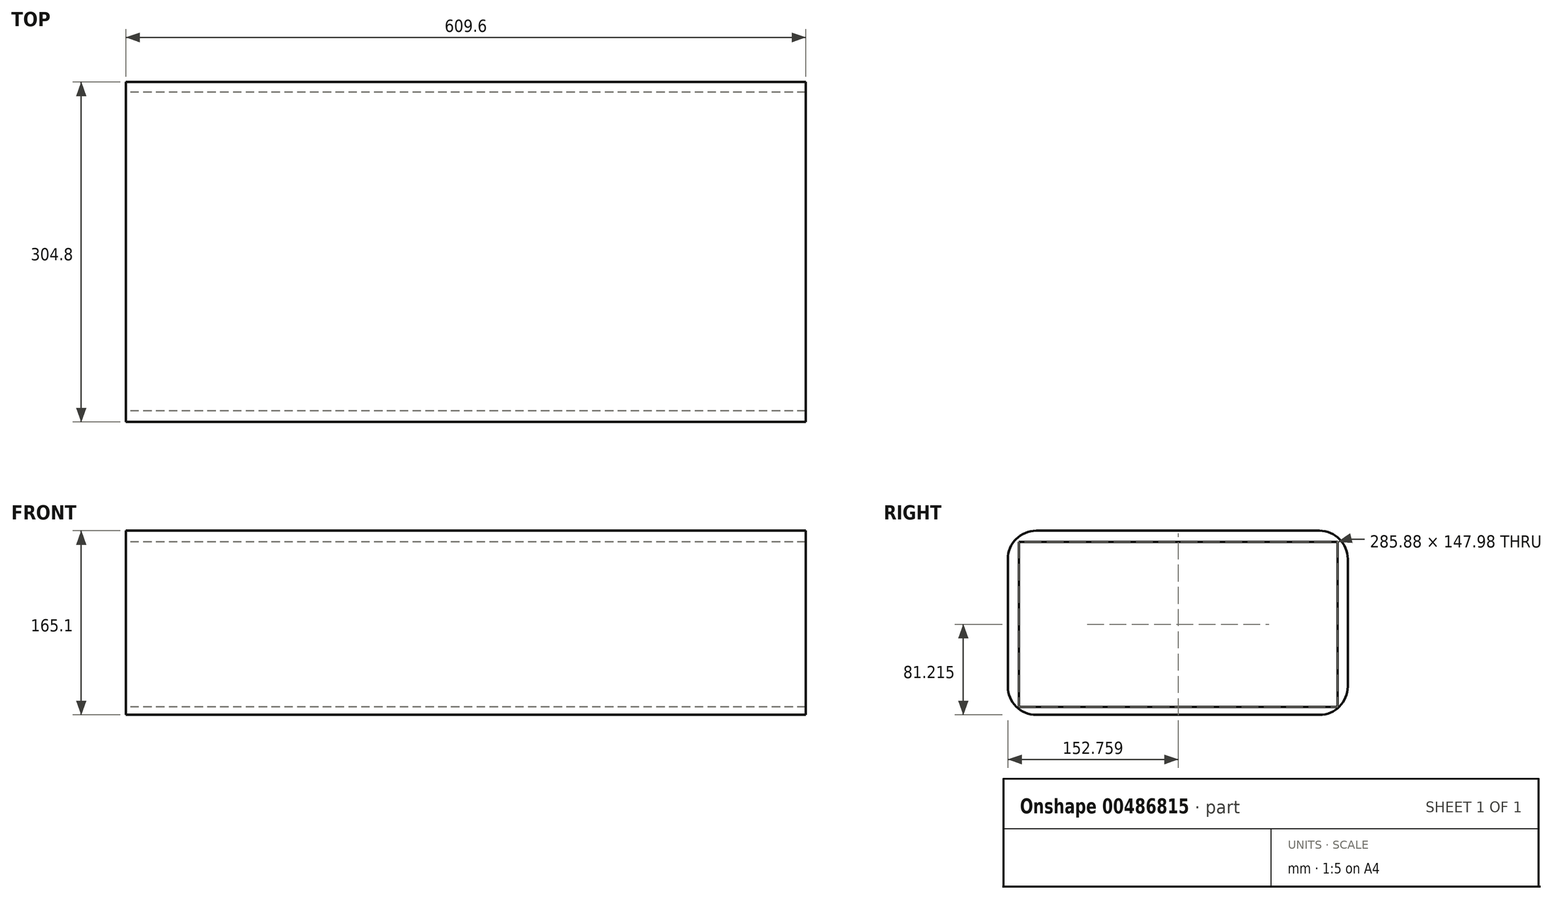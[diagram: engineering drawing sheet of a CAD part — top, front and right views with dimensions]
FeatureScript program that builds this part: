
annotation { "Feature Type Name" : "Feature", "Feature Type Description" : "" }
export const myFeature = defineFeature(function(context is Context, id is Id, definition is map)
    precondition{}
    {
        {
            var Q0;
            Q0=qCreatedBy(makeId("Right.planeOp"),FACE);
            var sketch = newSketch(context, id + "F0", { "sketchPlane" : qUnion([Q0])});
            skLineSegment(sketch, "E0.bottom", {"start": v(-140.28, 53.64) * mm, "end": v(164.52, 53.64) * mm});
            skLineSegment(sketch, "E0.top", {"start": v(-140.28, -111.46) * mm, "end": v(164.52, -111.46) * mm});
            skLineSegment(sketch, "E0.left", {"start": v(-140.28, 53.64) * mm, "end": v(-140.28, -111.46) * mm});
            skLineSegment(sketch, "E0.right", {"start": v(164.52, 53.64) * mm, "end": v(164.52, -111.46) * mm});
            skLineSegment(sketch, "E1.bottom", {"start": v(-130.46, 43.74) * mm, "end": v(155.42, 43.74) * mm});
            skLineSegment(sketch, "E1.top", {"start": v(-130.46, -104.24) * mm, "end": v(155.42, -104.24) * mm});
            skLineSegment(sketch, "E1.left", {"start": v(-130.46, 43.74) * mm, "end": v(-130.46, -104.24) * mm});
            skLineSegment(sketch, "E1.right", {"start": v(155.42, 43.74) * mm, "end": v(155.42, -104.24) * mm});
            skSolve(sketch);
        }
        {
            var Q0;
            Q0=makeQuery(id+"F0.imprint","IMPRINT",FACE,{"disambiguationData":[TD([[makeQuery(id+"F0.imprint","IMPRINT",EDGE,{"derivedFrom":sQuery(id+"F0.wireOp",EDGE,"E0.bottom")}),-1.0]])]});
            extrude(context, id + "F1", {"entities" : qUnion([Q0]), "depth" : 609.6 * mm, "offsetDistance" : 25.4 * mm});
        }
        {
            var Q0;
            Q0=makeQuery(id+"F1.opExtrude","SWEPT_EDGE",EDGE,{"disambiguationData":[OSD([sQuery(id+"F0.wireOp",EDGE,"E0.bottom"),sQuery(id+"F0.wireOp",EDGE,"E0.left")])]});
            var Q1;
            Q1=makeQuery(id+"F1.opExtrude","SWEPT_EDGE",EDGE,{"disambiguationData":[OSD([sQuery(id+"F0.wireOp",EDGE,"E0.bottom"),sQuery(id+"F0.wireOp",EDGE,"E0.right")])]});
            var Q2;
            Q2=makeQuery(id+"F1.opExtrude","SWEPT_EDGE",EDGE,{"disambiguationData":[OSD([sQuery(id+"F0.wireOp",EDGE,"E0.top"),sQuery(id+"F0.wireOp",EDGE,"E0.left")])]});
            var Q3;
            Q3=makeQuery(id+"F1.opExtrude","SWEPT_EDGE",EDGE,{"disambiguationData":[OSD([sQuery(id+"F0.wireOp",EDGE,"E0.top"),sQuery(id+"F0.wireOp",EDGE,"E0.right")])]});
            fillet(context, id + "F2", {"entities" : qUnion([Q0, Q1, Q2, Q3]), "radius" : 25.4 * mm, "tangentPropagation" : true, "allowEdgeOverflow" : false});
        }
    });
